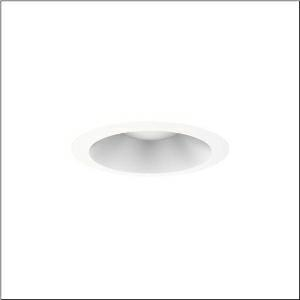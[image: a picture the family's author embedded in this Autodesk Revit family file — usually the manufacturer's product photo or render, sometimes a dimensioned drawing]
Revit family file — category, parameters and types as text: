
# Revit family: lunis_31-xl_51dn16mg32b
name_source: partatom
category: Lighting Fixtures
units: mm (PartAtom-declared; Revit-internal decimal feet)

## family parameters
Cut with Voids When Loaded = No
Host = Face
Light Source = No
Part Type = Normal
Room Calculation Point = No
Round Connector Dimension = Use Diameter
Shared = No

## types (1)
- --- (1 x LED, 2500 lm, 17 W, 3000K)
    Apparent Load = 17 VA
    CIE Flux Codes = 64 93 99 100 100
    Color Rendering = 80
    Color Temperature = 3000K
    Default Elevation = 1800 mm
    Description = Lunis 31-XL, downlight, light control with reflector, light emission: direct distribution, LED rated luminous flux: 2.500lm, light colour: 830, mains connection: 220..240V, AC/DC, 0/50..60Hz, housing, of aluminium, white, protection rating (complete): IP20, protection rating (on room side): IP54, insulation class (complete): insulation class II (safety insulation), certification: CE, ENEC, packaging unit: 1 piece
    Height = 0 mm  [stored 0 ft]
    Lamp = 1 x LED
    Lamp Light Flux = 2500 lm
    Lamp Power = 17 W
    Lamp count = 1
    Length = 259 mm
    Luminous efficacy = 147 lm/W
    Manufacturer = Siteco
    ModVariant = No
    Model = 51DN16MG32B
    Mounting Place = Ceiling
    Mounting Type = Recessed
    Number of Poles = 1
    OnlyDefault = Yes
    Power Factor = 1
    Product Name = Lunis 31-XL
    Product group = downlight
    ProductGroupID = 401
    Protection Class = Protection class II
    Protection Degree = IP 20
    RLX_Detail_Level = 1
    RLX_Emergency_Light_Flux = 0 lm
    RLX_Emergency_Type = 0
    RLX_Emergency_Type_DB = No
    RlxData = <blob elided: 24285 chars, md5=e82d7f91>
    Socket = socket
    Standby Power = 0 W
    System Light Flux = 2500 lm
    System Power = 17 W
    Type Comments = individual setting: luminous flux: 100 % | (ON | ON | ON | OFF) | 450 mA
    Type Image = l_1345915.jpg
    URL = http://relux.com
    VarID = @adj_029655
    Voltage = 0 V
    Weight = 0.00 kg
    Width = 0 mm  [stored 0 ft]

note: [stored X ft] marks values corroborated as IEEE doubles in the binary element streams (Revit-internal decimal feet)

## geometry (parser evidence)
native form markers: Blend x4, Sweep x9
no freeform markers — native parametric forms only
